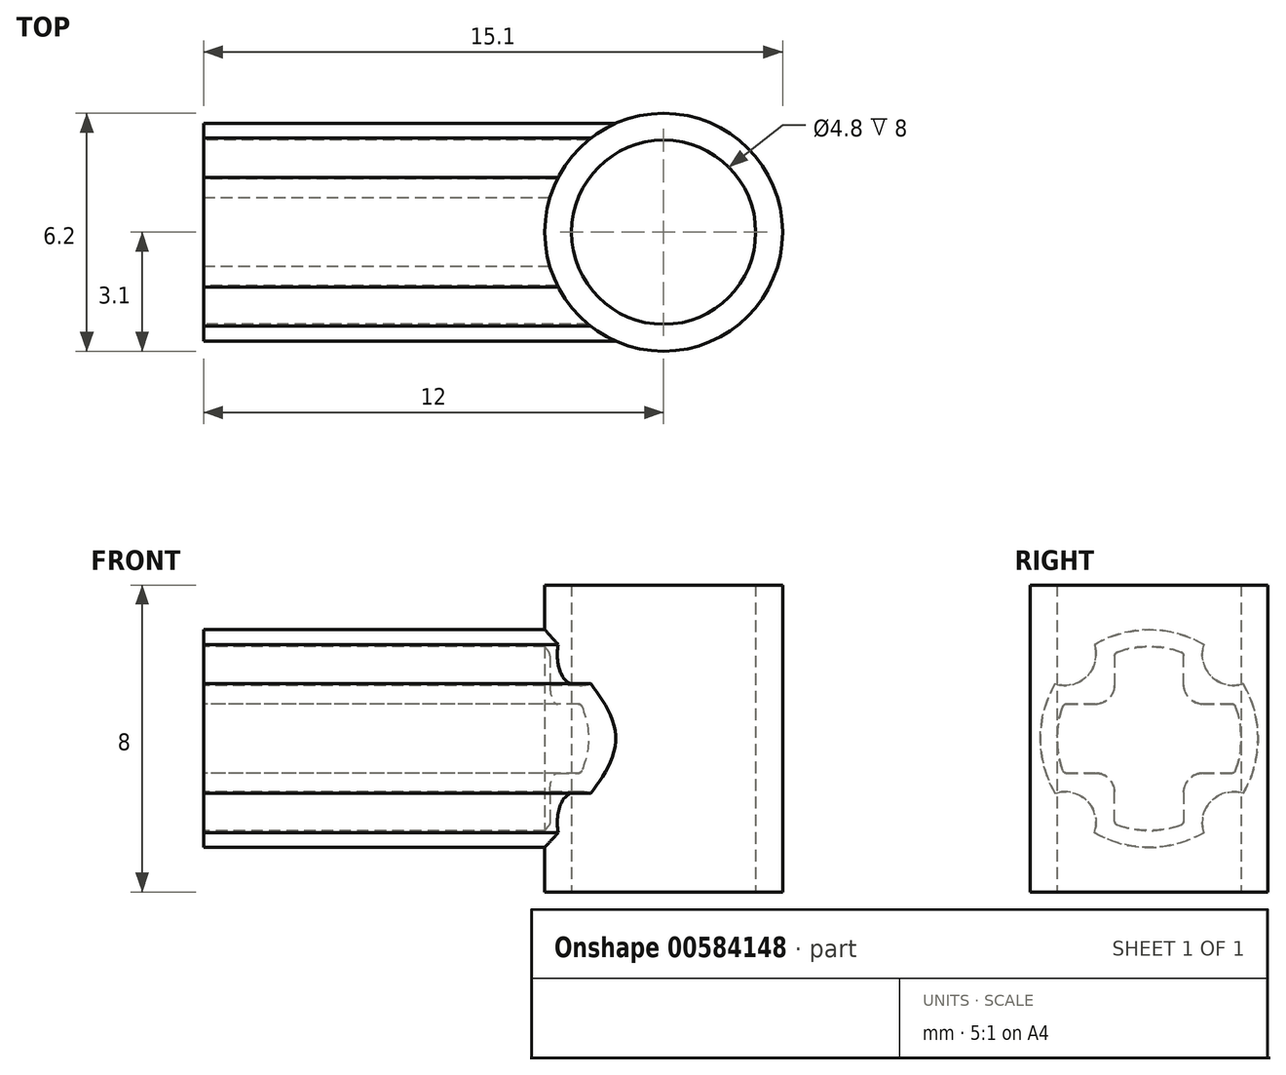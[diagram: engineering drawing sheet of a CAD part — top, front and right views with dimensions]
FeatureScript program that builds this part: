
annotation { "Feature Type Name" : "Feature", "Feature Type Description" : "" }
export const myFeature = defineFeature(function(context is Context, id is Id, definition is map)
    precondition{}
    {
        {
            var Q0;
            Q0=qCreatedBy(makeId("Top.planeOp"),FACE);
            var sketch = newSketch(context, id + "F0", { "sketchPlane" : qUnion([Q0])});
            skArc(sketch, "E0", {"start": v(0, 2.4) * mm, "mid": v(-2.4, 0) * mm, "end": v(0, -2.4) * mm});
            skArc(sketch, "E1", {"start": v(0, 3.1) * mm, "mid": v(-3.1, 0) * mm, "end": v(0, -3.1) * mm});
            skLineSegment(sketch, "E2", {"start": v(0, 3.1) * mm, "end": v(0, 2.4) * mm});
            skLineSegment(sketch, "E3", {"start": v(0, -2.4) * mm, "end": v(0, -3.1) * mm});
            skSolve(sketch);
        }
        {
            var Q0;
            Q0=qSketchRegion(id+"F0",true);
            extrude(context, id + "F1", {"entities" : qUnion([Q0]), "depth" : 4 * mm, "offsetDistance" : 25 * mm});
        }
        {
            var Q0;
            Q0=makeQuery(id+"F1.opExtrude","CAP_VERTEX",VERTEX,{"disambiguationData":[OSD([sQuery(id+"F0.wireOp",EDGE,"E1"),sQuery(id+"F0.wireOp",EDGE,"E2")])],"isStart":false});
            var Q1;
            Q1=makeQuery(id+"F1.opExtrude","CAP_VERTEX",VERTEX,{"disambiguationData":[OSD([sQuery(id+"F0.wireOp",EDGE,"E0"),sQuery(id+"F0.wireOp",EDGE,"E2")])],"isStart":false});
            var Q2;
            Q2=makeQuery(id+"F1.opExtrude","CAP_VERTEX",VERTEX,{"disambiguationData":[OSD([sQuery(id+"F0.wireOp",EDGE,"E0"),sQuery(id+"F0.wireOp",EDGE,"E2")])],"isStart":true});
            cPlane(context, id + "F2", {"entities" : qUnion([Q0, Q1, Q2]), "cplaneType" : CPlaneType.THREE_POINT, "offset" : 25 * mm, "width" : 150 * mm, "height" : 150 * mm});
        }
        {
            var Q0;
            Q0=qCreatedBy(id+"F2.planeOp",FACE);
            cPlane(context, id + "F3", {"entities" : qUnion([Q0]), "cplaneType" : CPlaneType.OFFSET, "offset" : 12 * mm, "width" : 150 * mm, "height" : 150 * mm});
        }
        {
            var Q0;
            Q0=qCreatedBy(id+"F3.planeOp",FACE);
            var sketch = newSketch(context, id + "F4", { "sketchPlane" : qUnion([Q0])});
            skLineSegment(sketch, "E4.0", {"start": v(2.4, 0) * mm, "end": v(3.1, 0) * mm, "construction": true});
            skLineSegment(sketch, "E4.1", {"start": v(-3.1, 0) * mm, "end": v(-2.4, 0) * mm, "construction": true});
            skLineSegment(sketch, "E5", {"start": v(-2.4, 0) * mm, "end": v(2.4, 0) * mm, "construction": true});
            skLineSegment(sketch, "E6", {"start": v(0, 1.65) * mm, "end": v(0, -0.27) * mm, "construction": true});
            skPoint(sketch, "E6.startSnap0", {"position": v(0, 0) * mm});
            skLineSegment(sketch, "E7", {"start": v(0, 5.29) * mm, "end": v(0, 1.3) * mm, "construction": true});
            skLineSegment(sketch, "E8.0", {"start": v(-0.9, 1.4) * mm, "end": v(-0.9, 2.16) * mm});
            skArc(sketch, "E8.1", {"start": v(-0.9, 2.16) * mm, "mid": v(-0.88, 2.21) * mm, "end": v(-0.83, 2.25) * mm});
            skArc(sketch, "E8.2", {"start": v(-0.83, 2.25) * mm, "mid": v(0, 2.4) * mm, "end": v(0.83, 2.25) * mm});
            skArc(sketch, "E8.3", {"start": v(0.83, 2.25) * mm, "mid": v(0.88, 2.21) * mm, "end": v(0.9, 2.16) * mm});
            skLineSegment(sketch, "E8.4", {"start": v(0.9, 2.16) * mm, "end": v(0.9, 1.4) * mm});
            skArc(sketch, "E8.5", {"start": v(0.9, 1.4) * mm, "mid": v(1.05, 1.05) * mm, "end": v(1.4, 0.9) * mm});
            skLineSegment(sketch, "E8.6", {"start": v(1.4, 0.9) * mm, "end": v(2.16, 0.9) * mm});
            skArc(sketch, "E8.7", {"start": v(-1.4, 0.9) * mm, "mid": v(-1.05, 1.05) * mm, "end": v(-0.9, 1.4) * mm});
            skLineSegment(sketch, "E8.8", {"start": v(-2.16, 0.9) * mm, "end": v(-1.4, 0.9) * mm});
            skArc(sketch, "E8.10", {"start": v(-2.25, 0.83) * mm, "mid": v(-2.21, 0.88) * mm, "end": v(-2.16, 0.9) * mm});
            skArc(sketch, "E8.11", {"start": v(2.16, 0.9) * mm, "mid": v(2.21, 0.88) * mm, "end": v(2.25, 0.83) * mm});
            skArc(sketch, "E8.12", {"start": v(2.25, 0.83) * mm, "mid": v(2.36, 0.42) * mm, "end": v(2.4, 0) * mm});
            skArc(sketch, "E9", {"start": v(-2.4, 0) * mm, "mid": v(-2.36, 0.42) * mm, "end": v(-2.25, 0.83) * mm});
            skArc(sketch, "E10.MirrorCS", {"start": v(-2.25, -0.83) * mm, "mid": v(-2.21, -0.88) * mm, "end": v(-2.16, -0.9) * mm});
            skArc(sketch, "E11.MirrorCS", {"start": v(2.16, -0.9) * mm, "mid": v(2.21, -0.88) * mm, "end": v(2.25, -0.83) * mm});
            skArc(sketch, "E12.MirrorCS", {"start": v(0.83, -2.25) * mm, "mid": v(0.88, -2.21) * mm, "end": v(0.9, -2.16) * mm});
            skArc(sketch, "E13.MirrorCS", {"start": v(-0.9, -2.16) * mm, "mid": v(-0.88, -2.21) * mm, "end": v(-0.83, -2.25) * mm});
            skLineSegment(sketch, "E14.MirrorCS", {"start": v(-2.16, -0.9) * mm, "end": v(-1.4, -0.9) * mm});
            skArc(sketch, "E15.MirrorCS", {"start": v(2.25, -0.83) * mm, "mid": v(2.36, -0.42) * mm, "end": v(2.4, 0) * mm});
            skArc(sketch, "E16.MirrorCS", {"start": v(-2.4, 0) * mm, "mid": v(-2.36, -0.42) * mm, "end": v(-2.25, -0.83) * mm});
            skLineSegment(sketch, "E17.MirrorCS", {"start": v(0, -1.65) * mm, "end": v(0, 0.27) * mm, "construction": true});
            skLineSegment(sketch, "E18.MirrorCS", {"start": v(0.9, -2.16) * mm, "end": v(0.9, -1.4) * mm});
            skLineSegment(sketch, "E19.MirrorCS", {"start": v(-0.9, -1.4) * mm, "end": v(-0.9, -2.16) * mm});
            skLineSegment(sketch, "E20.MirrorCS", {"start": v(0, -5.29) * mm, "end": v(0, -1.3) * mm, "construction": true});
            skArc(sketch, "E21.MirrorCS", {"start": v(-1.4, -0.9) * mm, "mid": v(-1.05, -1.05) * mm, "end": v(-0.9, -1.4) * mm});
            skArc(sketch, "E22.MirrorCS", {"start": v(0.9, -1.4) * mm, "mid": v(1.05, -1.05) * mm, "end": v(1.4, -0.9) * mm});
            skArc(sketch, "E23.MirrorCS", {"start": v(-0.83, -2.25) * mm, "mid": v(0, -2.4) * mm, "end": v(0.83, -2.25) * mm});
            skLineSegment(sketch, "E24.MirrorCS", {"start": v(1.4, -0.9) * mm, "end": v(2.16, -0.9) * mm});
            skArc(sketch, "E25", {"start": v(-2.84, 0) * mm, "mid": v(-2.74, 0.74) * mm, "end": v(-2.45, 1.43) * mm});
            skLineSegment(sketch, "E26", {"start": v(0, 0) * mm, "end": v(-2.67, 2.67) * mm, "construction": true});
            skArc(sketch, "E27", {"start": v(-2.45, 1.43) * mm, "mid": v(-2, 1.4) * mm, "end": v(-1.62, 1.62) * mm});
            skArc(sketch, "E28.MirrorCS", {"start": v(-1.43, 2.45) * mm, "mid": v(-1.4, 2) * mm, "end": v(-1.62, 1.62) * mm});
            skArc(sketch, "E29.MirrorCS", {"start": v(0, 2.84) * mm, "mid": v(-0.74, 2.74) * mm, "end": v(-1.43, 2.45) * mm});
            skArc(sketch, "E30.MirrorCS", {"start": v(0, 2.84) * mm, "mid": v(0.74, 2.74) * mm, "end": v(1.43, 2.45) * mm});
            skArc(sketch, "E31.MirrorCS", {"start": v(2.45, 1.43) * mm, "mid": v(2, 1.4) * mm, "end": v(1.62, 1.62) * mm});
            skArc(sketch, "E32.MirrorCS", {"start": v(1.43, 2.45) * mm, "mid": v(1.4, 2) * mm, "end": v(1.62, 1.62) * mm});
            skArc(sketch, "E33.MirrorCS", {"start": v(2.84, 0) * mm, "mid": v(2.74, 0.74) * mm, "end": v(2.45, 1.43) * mm});
            skArc(sketch, "E34.MirrorCS", {"start": v(-2.84, 0) * mm, "mid": v(-2.74, -0.74) * mm, "end": v(-2.45, -1.43) * mm});
            skArc(sketch, "E35.MirrorCS", {"start": v(-2.45, -1.43) * mm, "mid": v(-2, -1.4) * mm, "end": v(-1.62, -1.62) * mm});
            skArc(sketch, "E36.MirrorCS", {"start": v(-1.43, -2.45) * mm, "mid": v(-1.4, -2) * mm, "end": v(-1.62, -1.62) * mm});
            skArc(sketch, "E37.MirrorCS", {"start": v(0, -2.84) * mm, "mid": v(-0.74, -2.74) * mm, "end": v(-1.43, -2.45) * mm});
            skArc(sketch, "E38.MirrorCS", {"start": v(0, -2.84) * mm, "mid": v(0.74, -2.74) * mm, "end": v(1.43, -2.45) * mm});
            skArc(sketch, "E39.MirrorCS", {"start": v(1.43, -2.45) * mm, "mid": v(1.4, -2) * mm, "end": v(1.62, -1.62) * mm});
            skArc(sketch, "E40.MirrorCS", {"start": v(2.45, -1.43) * mm, "mid": v(2, -1.4) * mm, "end": v(1.62, -1.62) * mm});
            skArc(sketch, "E41.MirrorCS", {"start": v(2.84, 0) * mm, "mid": v(2.74, -0.74) * mm, "end": v(2.45, -1.43) * mm});
            skSolve(sketch);
        }
        {
            var Q0;
            Q0=makeQuery(id+"F1.opExtrude","SWEPT_BODY",BODY,{"disambiguationData":[OSD([sQuery(id+"F0.wireOp",EDGE,"E0"),sQuery(id+"F0.wireOp",EDGE,"E1"),sQuery(id+"F0.wireOp",EDGE,"E2"),sQuery(id+"F0.wireOp",EDGE,"E3")])]});
            var Q1;
            Q1=makeQuery(id+"F1.opExtrude","SWEPT_FACE",FACE,{"disambiguationData":[OSD([sQuery(id+"F0.wireOp",EDGE,"E2")])]});
            mirror(context, id + "F5", {"operationType" : NewBodyOperationType.ADD, "entities" : qUnion([Q0]), "mirrorPlane" : qUnion([Q1])});
        }
        {
            var Q0;
            Q0=makeQuery(id+"F1.opExtrude","SWEPT_BODY",BODY,{"disambiguationData":[OSD([sQuery(id+"F0.wireOp",EDGE,"E0"),sQuery(id+"F0.wireOp",EDGE,"E1"),sQuery(id+"F0.wireOp",EDGE,"E2"),sQuery(id+"F0.wireOp",EDGE,"E3")])]});
            var Q1;
            {var subQ0=makeQuery(id+"F1.opExtrude","CAP_FACE",FACE,{"disambiguationData":[OSD([sQuery(id+"F0.wireOp",EDGE,"E0"),sQuery(id+"F0.wireOp",EDGE,"E1"),sQuery(id+"F0.wireOp",EDGE,"E2"),sQuery(id+"F0.wireOp",EDGE,"E3")])],"isStart":true});Q1=makeQuery(id+"F5.boolean.opBoolean","MERGE",FACE,{"derivedFrom":[subQ0,makeQuery(id+"F5.opPattern","COPY",FACE,{"derivedFrom":subQ0,"instanceName":"1"})]});}
            mirror(context, id + "F6", {"operationType" : NewBodyOperationType.ADD, "entities" : qUnion([Q0]), "mirrorPlane" : qUnion([Q1])});
        }
        {
            var Q0;
            Q0=makeQuery(id+"F4.imprint","IMPRINT",FACE,{"disambiguationData":[TD([[makeQuery(id+"F4.imprint","IMPRINT",EDGE,{"derivedFrom":sQuery(id+"F4.wireOp",EDGE,"E8.0")}),1.0]])]});
            var Q1;
            Q1=makeQuery(id+"F1.opExtrude","SWEPT_BODY",BODY,{"disambiguationData":[OSD([sQuery(id+"F0.wireOp",EDGE,"E0"),sQuery(id+"F0.wireOp",EDGE,"E1"),sQuery(id+"F0.wireOp",EDGE,"E2"),sQuery(id+"F0.wireOp",EDGE,"E3")])]});
            extrude(context, id + "F7", {"entities" : qUnion([Q0]), "operationType" : NewBodyOperationType.ADD, "endBound" : BoundingType.UP_TO_BODY, "oppositeDirection" : true, "depth" : 25 * mm, "endBoundEntityBody" : qUnion([Q1]), "offsetDistance" : 25 * mm});
        }
    });
